# Revit family: Basin-Undercounter-American_Standard-Townsend-0330_Series
name_source: partatom
category: Plumbing Fixtures
revit_build: Autodesk Revit 2014 (Build: 20130308_1515(x64)
units: mm (PartAtom-declared; Revit-internal decimal feet)

## types (4) — shared parameters
ADA Compliant = Yes
Assembly Code = D2010310
Basin Shape = Rectangle
Bowl Depth = 4 1/2"
Bowl Length = 17 3/4"
Bowl Width = 11 5/8"
CW Connection = Yes
CWFU = 1.5
Cold Water Connection Diameter = 3/8"
Cold Water Connection Height = 23 1/2"
Cold Water Connection Radius = 3/16"
Default Elevation = 34"
Description = Townsend Under Counter Sink
HW Connection = Yes
HWFU = 1.5
Height = 6 1/2"
Hot Water Connection Diameter = 0"
Hot Water Connection Height = 23 1/2"
Hot Water Connection Radius = 3/16"
Installation Type = Undermount
Length = 19 1/2"
Manufacturer = American Standard
Price = Prices may vary. Please consult Manufacturer Representative for most up-to-date price list.
Revised Date = 12/10/2018
URL = http://www.americanstandard-us.com
Vent Connection = No
WFU = 2
Waste Connection = Yes
Waste Connection Diameter = 1 1/4"
Waste Connection Height = 21"
Waste Connection Radius = 5/8"
Width = 13 5/8"

## per-type parameters (varying)
| type | Finish | Material |
| 0330.000.020 | Vitreous China-American Standard-020-White | Vitreous China-American Standard-020-White |
| 0330.000.021 | Vitreous China-American Standard-021-Bone | Vitreous China-American Standard-021-Bone |
| 0330.000.178 | Vitreous China-American Standard-178-Black | Vitreous China-American Standard-178-Black |
| 0330.000.222 | Vitreous China-American Standard-222-Linen | Vitreous China-American Standard-222-Linen |

note: column(s) folded — value = type name in every type: Model

## geometry (parser evidence)
native form markers: Sweep x1
no freeform markers — native parametric forms only
